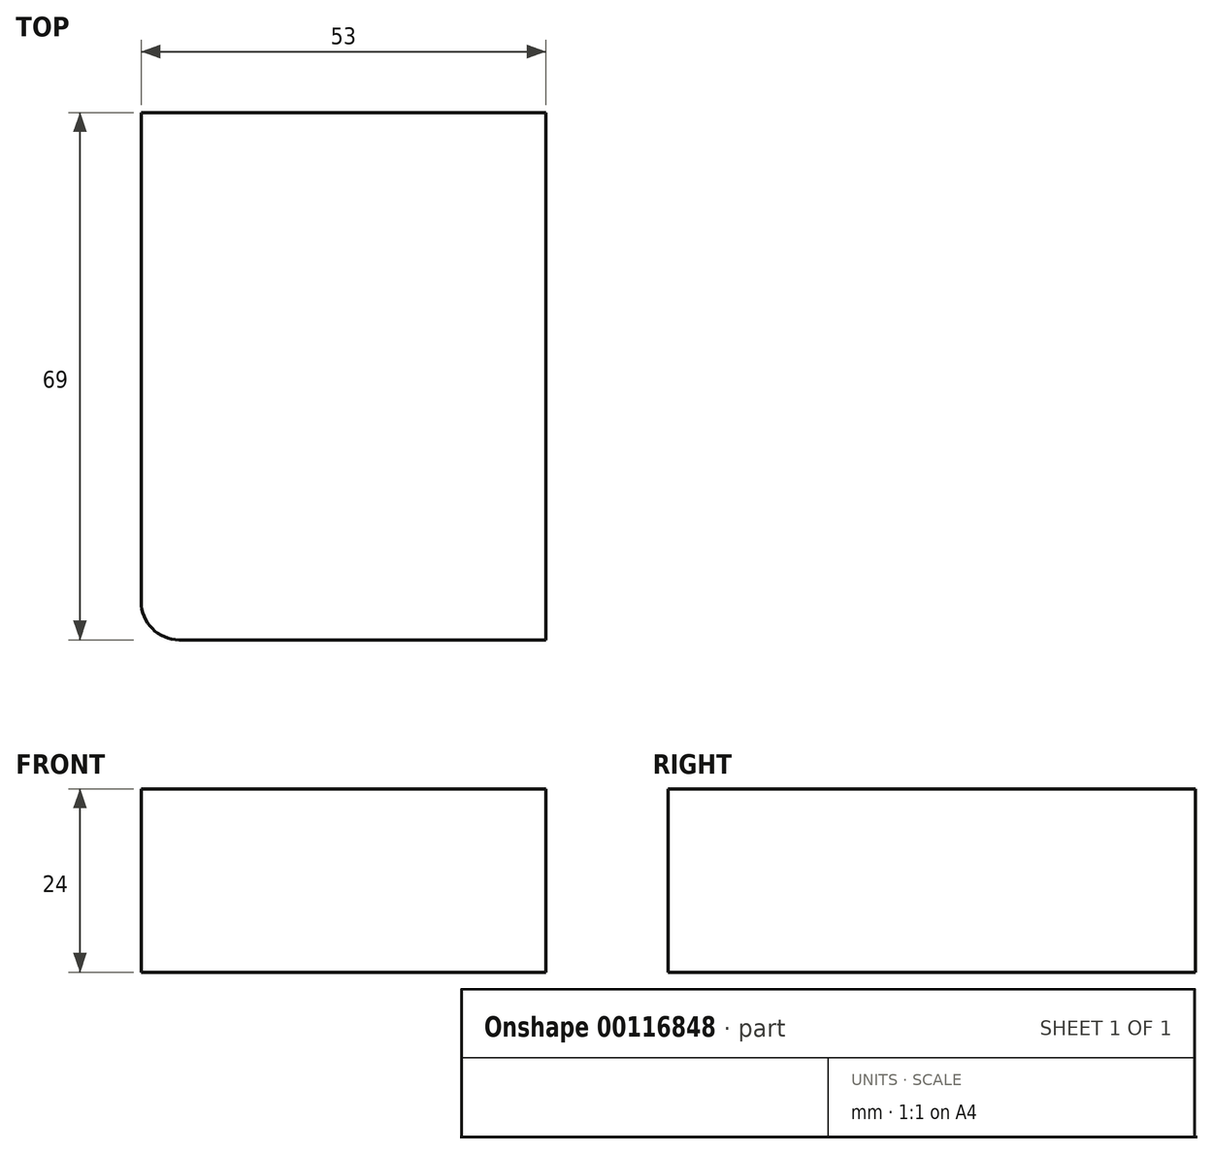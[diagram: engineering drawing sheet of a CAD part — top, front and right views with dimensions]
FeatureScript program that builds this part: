
annotation { "Feature Type Name" : "Feature", "Feature Type Description" : "" }
export const myFeature = defineFeature(function(context is Context, id is Id, definition is map)
    precondition{}
    {
        {
            var Q0;
            Q0=qCreatedBy(makeId("Front.planeOp"),FACE);
            var sketch = newSketch(context, id + "F0", { "sketchPlane" : qUnion([Q0])});
            skLineSegment(sketch, "E0.bottom", {"start": v(-43.17, 10.9) * mm, "end": v(9.83, 10.9) * mm});
            skLineSegment(sketch, "E0.top", {"start": v(-43.17, -13.1) * mm, "end": v(9.83, -13.1) * mm});
            skLineSegment(sketch, "E0.left", {"start": v(-43.17, 10.9) * mm, "end": v(-43.17, -13.1) * mm});
            skLineSegment(sketch, "E0.right", {"start": v(9.83, 10.9) * mm, "end": v(9.83, -13.1) * mm});
            skSolve(sketch);
        }
        {
            var Q0;
            Q0=qSketchRegion(id+"F0",true);
            extrude(context, id + "F1", {"entities" : qUnion([Q0]), "depth" : 69 * mm});
        }
        {
            var Q0;
            Q0=makeQuery(id+"F1.opExtrude","CAP_EDGE",EDGE,{"disambiguationData":[OSD([sQuery(id+"F0.wireOp",EDGE,"E0.left")])],"isStart":false});
            fillet(context, id + "F2", {"entities" : qUnion([Q0]), "radius" : 5 * mm, "tangentPropagation" : true, "allowEdgeOverflow" : false});
        }
    });
